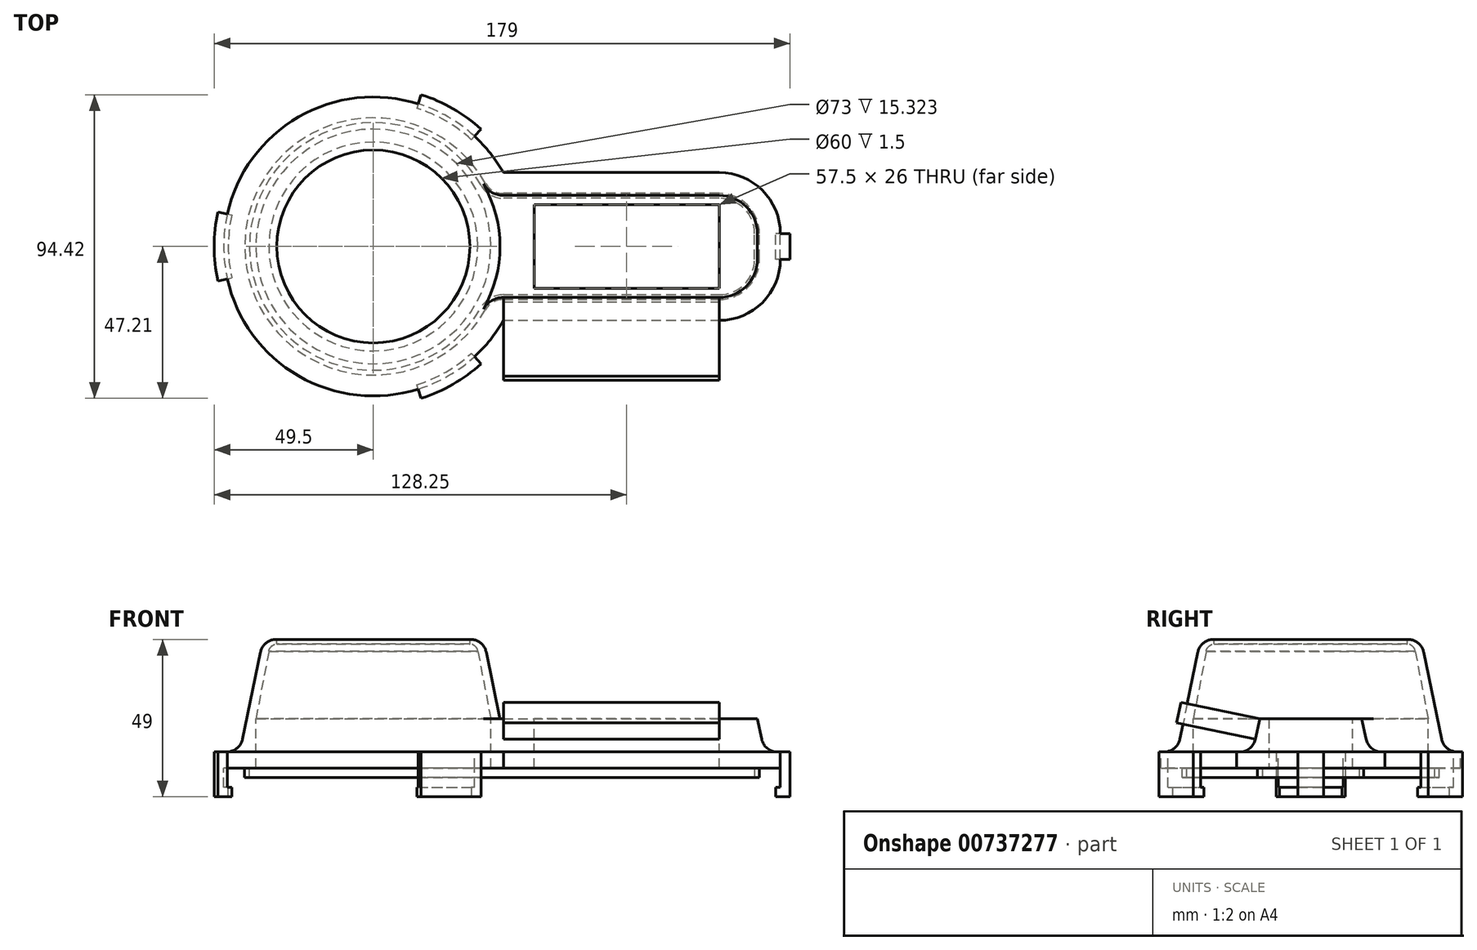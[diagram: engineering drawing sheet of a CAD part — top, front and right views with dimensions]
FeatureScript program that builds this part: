
annotation { "Feature Type Name" : "Feature", "Feature Type Description" : "" }
export const myFeature = defineFeature(function(context is Context, id is Id, definition is map)
    precondition{}
    {
        {
            var Q0;
            Q0=qCreatedBy(makeId("Top.planeOp"),FACE);
            var sketch = newSketch(context, id + "F0", { "sketchPlane" : qUnion([Q0])});
            skLineSegment(sketch, "E0", {"start": v(40.41, 6.5) * mm, "end": v(107.5, 6.5) * mm});
            skLineSegment(sketch, "E1", {"start": v(110, 4) * mm, "end": v(110, -4) * mm});
            skLineSegment(sketch, "E2", {"start": v(107.5, -6.5) * mm, "end": v(40.41, -6.5) * mm});
            skPoint(sketch, "E3.orphan", {"position": v(34.48, 0) * mm});
            skArc(sketch, "E4", {"start": v(26.07, 14.84) * mm, "mid": v(-4.47, 29.67) * mm, "end": v(-29.29, 6.5) * mm});
            skArc(sketch, "E5", {"start": v(26.07, -14.84) * mm, "mid": v(30, 0) * mm, "end": v(26.07, 14.84) * mm});
            skPoint(sketch, "E6.visualSharp", {"position": v(110, 6.5) * mm});
            skArc(sketch, "E6.filletArc", {"start": v(110, 4) * mm, "mid": v(109.27, 5.77) * mm, "end": v(107.5, 6.5) * mm});
            skPoint(sketch, "E7.visualSharp", {"position": v(110, -6.5) * mm});
            skArc(sketch, "E7.filletArc", {"start": v(107.5, -6.5) * mm, "mid": v(109.27, -5.77) * mm, "end": v(110, -4) * mm});
            skArc(sketch, "E8.filletArc", {"start": v(26.07, 14.84) * mm, "mid": v(32.12, 8.74) * mm, "end": v(40.41, 6.5) * mm});
            skArc(sketch, "E9.filletArc", {"start": v(40.41, -6.5) * mm, "mid": v(32.12, -8.74) * mm, "end": v(26.07, -14.84) * mm});
            skArc(sketch, "E10", {"start": v(-29.29, 6.5) * mm, "mid": v(-30, 0) * mm, "end": v(-29.29, -6.5) * mm});
            skArc(sketch, "E11", {"start": v(-29.29, -6.5) * mm, "mid": v(-10.79, -28) * mm, "end": v(17.35, -24.48) * mm});
            skArc(sketch, "E12", {"start": v(17.35, -24.48) * mm, "mid": v(22.24, -20.14) * mm, "end": v(26.07, -14.84) * mm});
            skLineSegment(sketch, "E13", {"start": v(17.35, 24.48) * mm, "end": v(17.35, 24.48) * mm});
            skSolve(sketch);
        }
        {
            var Q0;
            Q0=qCreatedBy(makeId("Front.planeOp"),FACE);
            var sketch = newSketch(context, id + "F1", { "sketchPlane" : qUnion([Q0])});
            skLineSegment(sketch, "E14", {"start": v(-46.58, 3) * mm, "end": v(-46.5, 3) * mm});
            skLineSegment(sketch, "E15", {"start": v(-43.7, 3) * mm, "end": v(-43.62, 3) * mm});
            skLineSegment(sketch, "E16", {"start": v(-38.5, 3) * mm, "end": v(-38.5, 0) * mm});
            skLineSegment(sketch, "E17", {"start": v(-38.5, 0) * mm, "end": v(-40, 0) * mm});
            skLineSegment(sketch, "E18", {"start": v(-40, 0) * mm, "end": v(-40, 3) * mm});
            skLineSegment(sketch, "E19", {"start": v(-45.57, 8) * mm, "end": v(-46.5, 8) * mm});
            skLineSegment(sketch, "E20", {"start": v(-46.5, 3) * mm, "end": v(-40, 3) * mm});
            skLineSegment(sketch, "E21", {"start": v(-38.5, 3) * mm, "end": v(-36.58, 3) * mm});
            skLineSegment(sketch, "E22", {"start": v(-30, 41.5) * mm, "end": v(-30, 43) * mm});
            skLineSegment(sketch, "E23", {"start": v(-30.2, 43) * mm, "end": v(-30, 43) * mm});
            skArc(sketch, "E24", {"start": v(-30, 41.5) * mm, "mid": v(-31.67, 40.86) * mm, "end": v(-32.48, 39.28) * mm});
            skArc(sketch, "E25.filletArc", {"start": v(-30.2, 43) * mm, "mid": v(-33.35, 41.88) * mm, "end": v(-35.09, 39.01) * mm});
            skLineSegment(sketch, "E26", {"start": v(-36.5, 3) * mm, "end": v(-36.5, 18.32) * mm});
            skLineSegment(sketch, "E27", {"start": v(-36.5, 18.32) * mm, "end": v(-39.37, 18.32) * mm});
            skLineSegment(sketch, "E28.trimOffspring", {"start": v(-39.37, 18.32) * mm, "end": v(-35.09, 39.01) * mm});
            skLineSegment(sketch, "E29", {"start": v(-32.48, 39.28) * mm, "end": v(-36.5, 18.32) * mm});
            skLineSegment(sketch, "E30", {"start": v(-40, 3) * mm, "end": v(-38.5, 3) * mm});
            skLineSegment(sketch, "E31", {"start": v(-40.68, 11.99) * mm, "end": v(-39.37, 18.32) * mm});
            skArc(sketch, "E32", {"start": v(-45.57, 8) * mm, "mid": v(-42.41, 9.12) * mm, "end": v(-40.68, 11.99) * mm});
            skLineSegment(sketch, "E33", {"start": v(-46.5, 8) * mm, "end": v(-46.5, 3) * mm});
            skLineSegment(sketch, "E34", {"start": v(-36.58, 3) * mm, "end": v(-36.5, 3) * mm});
            skLineSegment(sketch, "E35", {"start": v(-39.37, 18.32) * mm, "end": v(-39.37, 3) * mm});
            skLineSegment(sketch, "E36", {"start": v(-39.37, 3) * mm, "end": v(-39.37, 3) * mm});
            skSolve(sketch);
        }
        {
            var Q0;
            Q0=makeQuery(id+"F1.imprint","IMPRINT",FACE,{"disambiguationData":[TD([[makeQuery(id+"F1.imprint","IMPRINT",EDGE,{"derivedFrom":sQuery(id+"F1.wireOp",EDGE,"E19")}),1.0]])]});
            var Q1;
            Q1=makeQuery(id+"F1.imprint","IMPRINT",FACE,{"disambiguationData":[TD([[makeQuery(id+"F1.imprint","IMPRINT",EDGE,{"derivedFrom":sQuery(id+"F1.wireOp",EDGE,"E16")}),-1.0]])]});
            var Q2;
            {var subQ1=sQuery(id+"F1.wireOp",EDGE,"E21");Q2=makeQuery(id+"F1.imprint","IMPRINT",FACE,{"disambiguationData":[TD([[makeQuery(id+"F1.imprint","IMPRINT",EDGE,{"derivedFrom":subQ1}),1.0]])]});}
            var Q3;
            Q3=sQuery(id+"F0.wireOp",EDGE,"E4");
            var Q4;
            Q4=sQuery(id+"F0.wireOp",EDGE,"E2");
            var Q5;
            Q5=sQuery(id+"F0.wireOp",EDGE,"E1");
            var Q6;
            Q6=sQuery(id+"F0.wireOp",EDGE,"E0");
            var Q7;
            Q7=sQuery(id+"F0.wireOp",EDGE,"E6.filletArc");
            var Q8;
            Q8=sQuery(id+"F0.wireOp",EDGE,"E7.filletArc");
            var Q9;
            Q9=sQuery(id+"F0.wireOp",EDGE,"E8.filletArc");
            var Q10;
            Q10=sQuery(id+"F0.wireOp",EDGE,"E9.filletArc");
            var Q11;
            Q11=sQuery(id+"F0.wireOp",EDGE,"E10");
            var Q12;
            Q12=sQuery(id+"F0.wireOp",EDGE,"E11");
            var Q13;
            Q13=sQuery(id+"F0.wireOp",EDGE,"E12");
            sweep(context, id + "F2", {"profiles" : qUnion([Q0, Q1, Q2]), "path" : qUnion([Q3, Q4, Q5, Q6, Q7, Q8, Q9, Q10, Q11, Q12, Q13])});
        }
        {
            var Q0;
            Q0=makeQuery(id+"F1.imprint","IMPRINT",FACE,{"disambiguationData":[TD([[makeQuery(id+"F1.imprint","IMPRINT",EDGE,{"derivedFrom":sQuery(id+"F1.wireOp",EDGE,"E22")}),1.0]])]});
            var Q1;
            {var subQ1=sQuery(id+"F1.wireOp",EDGE,"E21");Q1=makeQuery(id+"F1.imprint","IMPRINT",FACE,{"disambiguationData":[TD([[makeQuery(id+"F1.imprint","IMPRINT",EDGE,{"derivedFrom":subQ1}),1.0]])]});}
            var Q2;
            Q2=sQuery(id+"F0.wireOp",EDGE,"E5");
            var Q3;
            Q3=sQuery(id+"F0.wireOp",EDGE,"E4");
            var Q4;
            Q4=sQuery(id+"F0.wireOp",EDGE,"E10");
            var Q5;
            Q5=sQuery(id+"F0.wireOp",EDGE,"E11");
            var Q6;
            Q6=sQuery(id+"F0.wireOp",EDGE,"E12");
            sweep(context, id + "F3", {"operationType" : NewBodyOperationType.ADD, "profiles" : qUnion([Q0, Q1]), "path" : qUnion([Q2, Q3, Q4, Q5, Q6])});
        }
        {
            var Q0;
            Q0=qCreatedBy(makeId("Right.planeOp"),FACE);
            cPlane(context, id + "F4", {"entities" : qUnion([Q0]), "cplaneType" : CPlaneType.OFFSET, "offset" : 50 * mm, "width" : 150 * mm, "height" : 150 * mm});
        }
        {
            var Q0;
            Q0=qCreatedBy(id+"F4.planeOp",FACE);
            var sketch = newSketch(context, id + "F5", { "sketchPlane" : qUnion([Q0])});
            skLineSegment(sketch, "E37.0.0", {"start": v(-13.63, 3) * mm, "end": v(13.63, 3) * mm});
            skLineSegment(sketch, "E37.0.1", {"start": v(13.63, 3) * mm, "end": v(13.63, 18.32) * mm});
            skLineSegment(sketch, "E37.0.2", {"start": v(13.63, 18.32) * mm, "end": v(-13.63, 18.32) * mm});
            skLineSegment(sketch, "E37.0.3", {"start": v(-13.63, 18.32) * mm, "end": v(-13.63, 3) * mm});
            skSolve(sketch);
        }
        {
            var Q0;
            Q0 = qSketchRegion(id + "F5", true);
            var Q1;
            Q1=makeQuery(id+"F3.opSweep","SWEPT_FACE",FACE,{"disambiguationData":[OSD([sQuery(id+"F0.wireOp",EDGE,"E4"),sQuery(id+"F1.wireOp",EDGE,"E35")])]});
            extrude(context, id + "F6", {"entities" : qUnion([Q0]), "operationType" : NewBodyOperationType.ADD, "endBound" : BoundingType.UP_TO_SURFACE, "oppositeDirection" : true, "depth" : 25 * mm, "endBoundEntityFace" : qUnion([Q1]), "offsetDistance" : 25 * mm});
        }
        {
            var Q0;
            Q0=makeQuery(id+"F2.opSweep","SWEPT_FACE",FACE,{"disambiguationData":[OSD([sQuery(id+"F0.wireOp",EDGE,"E1"),sQuery(id+"F1.wireOp",EDGE,"E26")])]});
            cPlane(context, id + "F7", {"entities" : qUnion([Q0]), "cplaneType" : CPlaneType.OFFSET, "offset" : 9 * mm, "width" : 150 * mm, "height" : 150 * mm});
        }
        {
            var Q0;
            Q0=qCreatedBy(id+"F7.planeOp",FACE);
            var sketch = newSketch(context, id + "F8", { "sketchPlane" : qUnion([Q0])});
            skLineSegment(sketch, "E38.0.0", {"start": v(13, 3) * mm, "end": v(-13, 3) * mm});
            skLineSegment(sketch, "E38.0.1", {"start": v(-13, 3) * mm, "end": v(-13, 18.32) * mm});
            skLineSegment(sketch, "E38.0.2", {"start": v(-13, 18.32) * mm, "end": v(13, 18.32) * mm});
            skLineSegment(sketch, "E38.0.3", {"start": v(13, 18.32) * mm, "end": v(13, 3) * mm});
            skSolve(sketch);
        }
        {
            var Q0;
            Q0 = qSketchRegion(id + "F8", true);
            var Q1;
            Q1=makeQuery(id+"F2.opSweep","SWEPT_FACE",FACE,{"disambiguationData":[OSD([sQuery(id+"F0.wireOp",EDGE,"E1"),sQuery(id+"F1.wireOp",EDGE,"E26")])]});
            var Q2;
            Q2=makeQuery(id+"F2.opSweep","SWEPT_BODY",BODY,{"disambiguationData":[OSD([sQuery(id+"F0.wireOp",EDGE,"E9.filletArc"),sQuery(id+"F1.wireOp",EDGE,"E16"),sQuery(id+"F1.wireOp",EDGE,"E17"),sQuery(id+"F1.wireOp",EDGE,"E18"),sQuery(id+"F1.wireOp",EDGE,"E19"),sQuery(id+"F1.wireOp",EDGE,"E20"),sQuery(id+"F1.wireOp",EDGE,"E21"),sQuery(id+"F1.wireOp",EDGE,"E26"),sQuery(id+"F1.wireOp",EDGE,"E27"),sQuery(id+"F1.wireOp",EDGE,"E31"),sQuery(id+"F1.wireOp",EDGE,"E32"),sQuery(id+"F1.wireOp",EDGE,"E33"),sQuery(id+"F1.wireOp",EDGE,"E34")])]});
            extrude(context, id + "F9", {"entities" : qUnion([Q0]), "operationType" : NewBodyOperationType.ADD, "endBound" : BoundingType.UP_TO_BODY, "oppositeDirection" : true, "depth" : 25 * mm, "endBoundEntityFace" : qUnion([Q1]), "endBoundEntityBody" : qUnion([Q2]), "offsetDistance" : 25 * mm});
        }
        {
            var Q0;
            Q0=qCreatedBy(makeId("Front.planeOp"),FACE);
            var sketch = newSketch(context, id + "F10", { "sketchPlane" : qUnion([Q0])});
            skLineSegment(sketch, "E39.0", {"start": v(-46.5, 8) * mm, "end": v(-46.5, 3) * mm});
            skLineSegment(sketch, "E40.0", {"start": v(40.41, 8) * mm, "end": v(40.41, 8) * mm});
            skLineSegment(sketch, "E41.right", {"start": v(-49.5, 8) * mm, "end": v(-49.5, -6) * mm});
            skLineSegment(sketch, "E42.bottom", {"start": v(-46.5, -3) * mm, "end": v(-45.09, -3) * mm});
            skLineSegment(sketch, "E42.top", {"start": v(-49.5, -6) * mm, "end": v(-45.09, -6) * mm});
            skLineSegment(sketch, "E43", {"start": v(-45.09, -3) * mm, "end": v(-45.09, -6) * mm});
            skLineSegment(sketch, "E44", {"start": v(-46.5, -3) * mm, "end": v(-46.5, 8) * mm});
            skLineSegment(sketch, "E45", {"start": v(-49.5, 8) * mm, "end": v(-46.5, 8) * mm});
            skSolve(sketch);
        }
        {
            var Q0;
            Q0=makeQuery(id+"F10.imprint","IMPRINT",FACE,{"disambiguationData":[TD([[makeQuery(id+"F10.imprint","IMPRINT",EDGE,{"derivedFrom":sQuery(id+"F10.wireOp",EDGE,"E41.right")}),1.0]])]});
            var Q1;
            Q1=sQuery(id+"F0.wireOp",EDGE,"E10");
            sweep(context, id + "F11", {"profiles" : qUnion([Q0]), "path" : qUnion([Q1])});
        }
        {
            var Q0;
            Q0=makeQuery(id+"F11.opSweep","SWEPT_BODY",BODY,{"disambiguationData":[OSD([sQuery(id+"F0.wireOp",EDGE,"E10"),sQuery(id+"F10.wireOp",EDGE,"E41.right"),sQuery(id+"F10.wireOp",EDGE,"E42.bottom"),sQuery(id+"F10.wireOp",EDGE,"E42.top"),sQuery(id+"F10.wireOp",EDGE,"E43"),sQuery(id+"F10.wireOp",EDGE,"E44"),sQuery(id+"F10.wireOp",EDGE,"E45")])]});
            var Q1;
            Q1=makeQuery(id+"F2.opSweep","SWEPT_FACE",FACE,{"disambiguationData":[OSD([sQuery(id+"F0.wireOp",EDGE,"E10"),sQuery(id+"F1.wireOp",EDGE,"E33")])]});
            circularPattern(context, id + "F12", {"operationType" : NewBodyOperationType.ADD, "entities" : qUnion([Q0]), "axis" : qUnion([Q1]), "angle" : 360 * degree, "instanceCount" : 3, "equalSpace" : true});
        }
        {
            var Q0;
            Q0=qCreatedBy(makeId("Front.planeOp"),FACE);
            var sketch = newSketch(context, id + "F13", { "sketchPlane" : qUnion([Q0])});
            skPoint(sketch, "E46.0", {"position": v(120.94, 8) * mm});
            skPoint(sketch, "E47.0", {"position": v(120.94, 3) * mm});
            skPoint(sketch, "E48.0", {"position": v(126.5, 5.5) * mm});
            skLineSegment(sketch, "E49.0", {"start": v(126.5, 8) * mm, "end": v(126.5, 3) * mm});
            skLineSegment(sketch, "E50.0", {"start": v(107.5, 8) * mm, "end": v(126.5, 8) * mm});
            skLineSegment(sketch, "E51.0", {"start": v(107.5, 3) * mm, "end": v(126.5, 3) * mm});
            skLineSegment(sketch, "E52.right", {"start": v(129.5, 8) * mm, "end": v(129.5, -6) * mm});
            skLineSegment(sketch, "E53.MirrorCS", {"start": v(129.5, 8) * mm, "end": v(126.5, 8) * mm});
            skLineSegment(sketch, "E54.MirrorCS", {"start": v(126.5, -3) * mm, "end": v(125.09, -3) * mm});
            skLineSegment(sketch, "E55.MirrorCS", {"start": v(125.09, -3) * mm, "end": v(125.09, -6) * mm});
            skLineSegment(sketch, "E56.MirrorCS", {"start": v(129.5, -6) * mm, "end": v(125.09, -6) * mm});
            skLineSegment(sketch, "E57", {"start": v(126.5, 8) * mm, "end": v(126.5, -3) * mm});
            skSolve(sketch);
        }
        {
            var Q0;
            Q0=makeQuery(id+"F13.imprint","IMPRINT",FACE,{"disambiguationData":[TD([[makeQuery(id+"F13.imprint","IMPRINT",EDGE,{"derivedFrom":sQuery(id+"F13.wireOp",EDGE,"E49.0")}),1.0]])]});
            extrude(context, id + "F14", {"entities" : qUnion([Q0]), "operationType" : NewBodyOperationType.ADD, "endBound" : BoundingType.SYMMETRIC, "depth" : 8 * mm, "offsetDistance" : 25 * mm});
        }
        {
            var Q0;
            Q0=makeQuery(id+"F2.opSweep","SWEPT_FACE",FACE,{"disambiguationData":[OSD([sQuery(id+"F0.wireOp",EDGE,"E2"),sQuery(id+"F1.wireOp",EDGE,"E31")])]});
            extrude(context, id + "F15", {"entities" : qUnion([Q0]), "operationType" : NewBodyOperationType.ADD, "depth" : 25 * mm, "offsetDistance" : 25 * mm});
        }
    });
